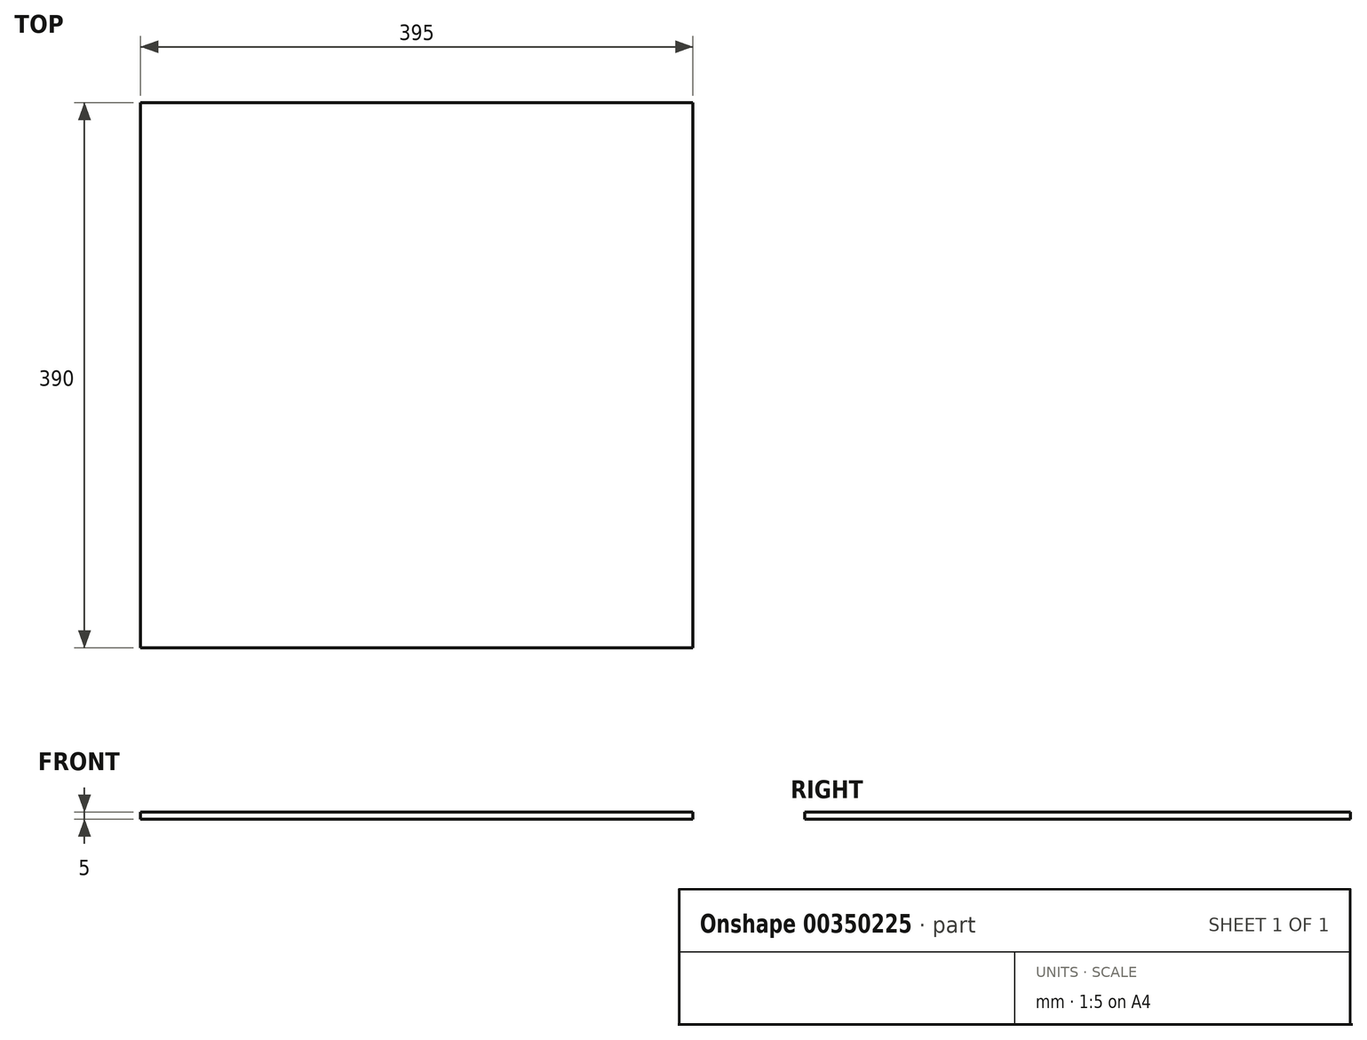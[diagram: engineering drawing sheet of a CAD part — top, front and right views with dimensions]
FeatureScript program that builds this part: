
annotation { "Feature Type Name" : "Feature", "Feature Type Description" : "" }
export const myFeature = defineFeature(function(context is Context, id is Id, definition is map)
    precondition{}
    {
        {
            var Q0;
            Q0=qCreatedBy(makeId("Front.planeOp"),FACE);
            var sketch = newSketch(context, id + "F0", { "sketchPlane" : qUnion([Q0])});
            skLineSegment(sketch, "E0.bottom", {"start": v(197.5, -2.5) * mm, "end": v(-197.5, -2.5) * mm});
            skLineSegment(sketch, "E0.top", {"start": v(197.5, 2.5) * mm, "end": v(-197.5, 2.5) * mm});
            skLineSegment(sketch, "E0.left", {"start": v(197.5, -2.5) * mm, "end": v(197.5, 2.5) * mm});
            skLineSegment(sketch, "E0.right", {"start": v(-197.5, -2.5) * mm, "end": v(-197.5, 2.5) * mm});
            skPoint(sketch, "E0.middle", {"position": v(0, 0) * mm});
            skSolve(sketch);
        }
        {
            var Q0;
            Q0 = qSketchRegion(id + "F0", true);
            extrude(context, id + "F1", {"entities" : qUnion([Q0]), "depth" : 390 * mm});
        }
    });
